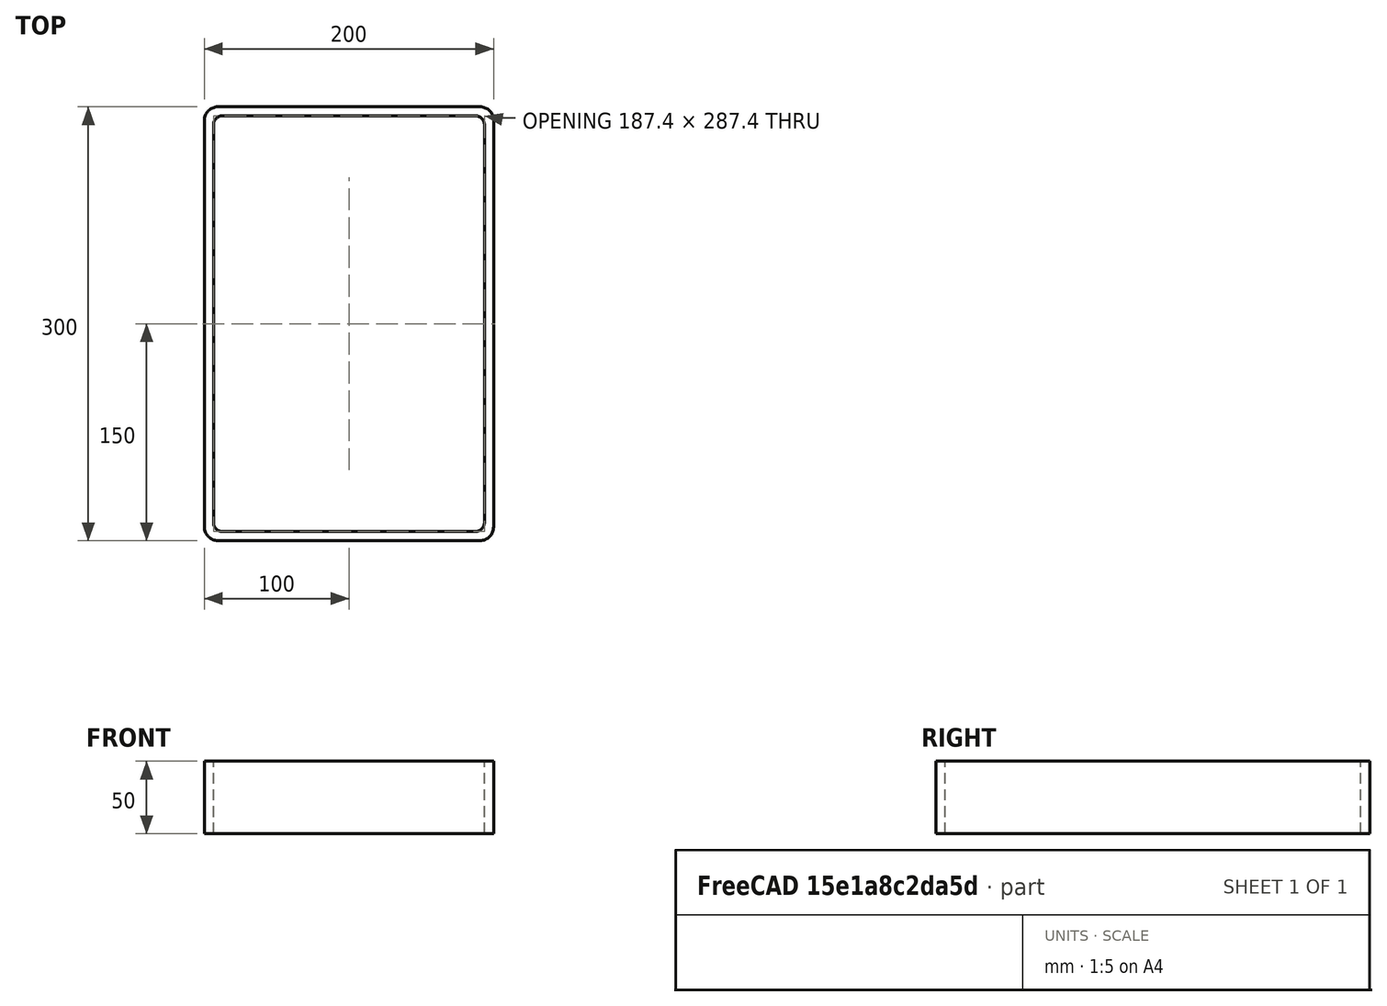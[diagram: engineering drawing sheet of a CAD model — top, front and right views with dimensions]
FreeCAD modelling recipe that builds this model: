
FCSTD DOCUMENT  (FreeCAD 0.15R4671 (Git))
Label: Rectangular hollow section 300x200x6.3 EN10219 S235JRH
License: All rights reserved
LicenseURL: http://en.wikipedia.org/wiki/All_rights_reserved
objects: Sketcher::SketchObject×1, Part::Extrusion×1
note: 2 computed .brp shape members not serialized (recipe doc carries the construction recipe); baked Part::Feature solids carry a one-line shape summary decoded from their .brp

FEATURE [Sketcher::SketchObject] Sketch
  sketch-geometry (16):
    g0: LineSegment StartX=-87.4 StartY=143.7 StartZ=0 EndX=87.4 EndY=143.7 EndZ=0
    g1: LineSegment StartX=93.7 StartY=137.4 StartZ=0 EndX=93.7 EndY=-137.4 EndZ=0
    g2: LineSegment StartX=87.4 StartY=-143.7 StartZ=0 EndX=-87.4 EndY=-143.7 EndZ=0
    g3: LineSegment StartX=-93.7 StartY=-137.4 StartZ=0 EndX=-93.7 EndY=137.4 EndZ=0
    g4: LineSegment StartX=-90.55 StartY=150 StartZ=0 EndX=90.55 EndY=150 EndZ=0
    g5: LineSegment StartX=100 StartY=140.55 StartZ=0 EndX=100 EndY=-140.55 EndZ=0
    g6: LineSegment StartX=90.55 StartY=-150 StartZ=0 EndX=-90.55 EndY=-150 EndZ=0
    g7: LineSegment StartX=-100 StartY=-140.55 StartZ=0 EndX=-100 EndY=140.55 EndZ=0
    g8: ArcOfCircle CenterX=-87.4 CenterY=137.4 CenterZ=0 NormalX=0 NormalY=0 NormalZ=1 Radius=6.3 StartAngle=1.5708 EndAngle=3.14159
    g9: ArcOfCircle CenterX=87.4 CenterY=137.4 CenterZ=0 NormalX=0 NormalY=0 NormalZ=1 Radius=6.3 StartAngle=0 EndAngle=1.5708
    g10: ArcOfCircle CenterX=87.4 CenterY=-137.4 CenterZ=0 NormalX=0 NormalY=0 NormalZ=1 Radius=6.3 StartAngle=4.71239 EndAngle=6.28319
    g11: ArcOfCircle CenterX=-87.4 CenterY=-137.4 CenterZ=0 NormalX=0 NormalY=0 NormalZ=1 Radius=6.3 StartAngle=3.14159 EndAngle=4.71239
    g12: ArcOfCircle CenterX=90.55 CenterY=140.55 CenterZ=0 NormalX=0 NormalY=0 NormalZ=1 Radius=9.45 StartAngle=0 EndAngle=1.5708
    g13: ArcOfCircle CenterX=90.55 CenterY=-140.55 CenterZ=0 NormalX=0 NormalY=0 NormalZ=1 Radius=9.45 StartAngle=4.71239 EndAngle=6.28319
    g14: ArcOfCircle CenterX=-90.55 CenterY=-140.55 CenterZ=0 NormalX=0 NormalY=0 NormalZ=1 Radius=9.45 StartAngle=3.14159 EndAngle=4.71239
    g15: ArcOfCircle CenterX=-90.55 CenterY=140.55 CenterZ=0 NormalX=0 NormalY=0 NormalZ=1 Radius=9.45 StartAngle=1.5708 EndAngle=3.14159
  constraints (36):
    c: Horizontal(g2)
    c: Vertical(g3)
    c: Horizontal(g6)
    c: Vertical(g7)
    c: Tangent(g3,g8) = 1.5708
    c: Tangent(g0,g8) = 1.5708
    c: Tangent(g0,g9) = 1.5708
    c: Tangent(g1,g9) = 1.5708
    c: Tangent(g1,g10) = 1.5708
    c: Tangent(g2,g10) = 1.5708
    c: Tangent(g2,g11) = 1.5708
    c: Tangent(g3,g11) = 1.5708
    c: Tangent(g4,g12) = 1.5708
    c: Tangent(g5,g12) = 1.5708
    c: Tangent(g5,g13) = 1.5708
    c: Tangent(g6,g13) = 1.5708
    c: Tangent(g6,g14) = 1.5708
    c: Tangent(g7,g14) = 1.5708
    c: Tangent(g7,g15) = 1.5708
    c: Tangent(g4,g15) = 1.5708
    c: Equal(g9,g8)
    c: Equal(g9,g11)
    c: Equal(g9,g10)
    c: Equal(g12,g15)
    c: Equal(g12,g14)
    c: Equal(g12,g13)
    c: Symmetric(g4,g6,g-1)
    c: Symmetric(g7,g5,g-2)
    c: DistanceY(g4,g6) = -300
    c: DistanceX(g7,g5) = 200
    c: Symmetric(g3,g1,g-2)
    c: Symmetric(g0,g2,g-1)
    c: DistanceY(g0,g4) = 6.3
    c: DistanceX(g5,g1) = -6.3
    c: Radius(g9) = 6.3
    c: Radius(g12) = 9.45
FEATURE [Part::Extrusion] Extrude  label="Rectangular hollow section 300x200x6.3 EN10219 S235JRH"
  Base = -> Sketch
  Dir = (0,0,50)
  Solid = true
